# Revit family: FU_Inspec_Addit_9-4
name_source: partatom
category: Furniture
units: mm (PartAtom-declared; Revit-internal decimal feet)

## family parameters
Always vertical = Yes
Cut with Voids When Loaded = No
OmniClass Number = 23.40.20.00
OmniClass Title = General Furniture and Specialties
Room Calculation Point = No
Shared = No
Work Plane-Based = No

## types (2) — shared parameters
Assembly Code = E2020
Back Material = Fabric - Green
Description = Modular sofa unit on legs of powder coated or chromium plated cast aluminium. Corner unit with upholstered seat and back and built-in magnetic linking device.
Keynote = 46.B
Legs Material = Metal - Chrome - Polished
Manufacturer = Inspec
Model = addit 9.4
Seat Material = Fabric - Green
URL = https://inspecfurniture.com
zero-valued in all types: Default Elevation

## per-type parameters (varying)
| type | Frame Material |
| 1 Colour | Fabric - Green |
| 2 Color | Fabric - White |

## geometry (parser evidence)
native form markers: Blend x8, Sweep x3
no freeform markers — native parametric forms only
